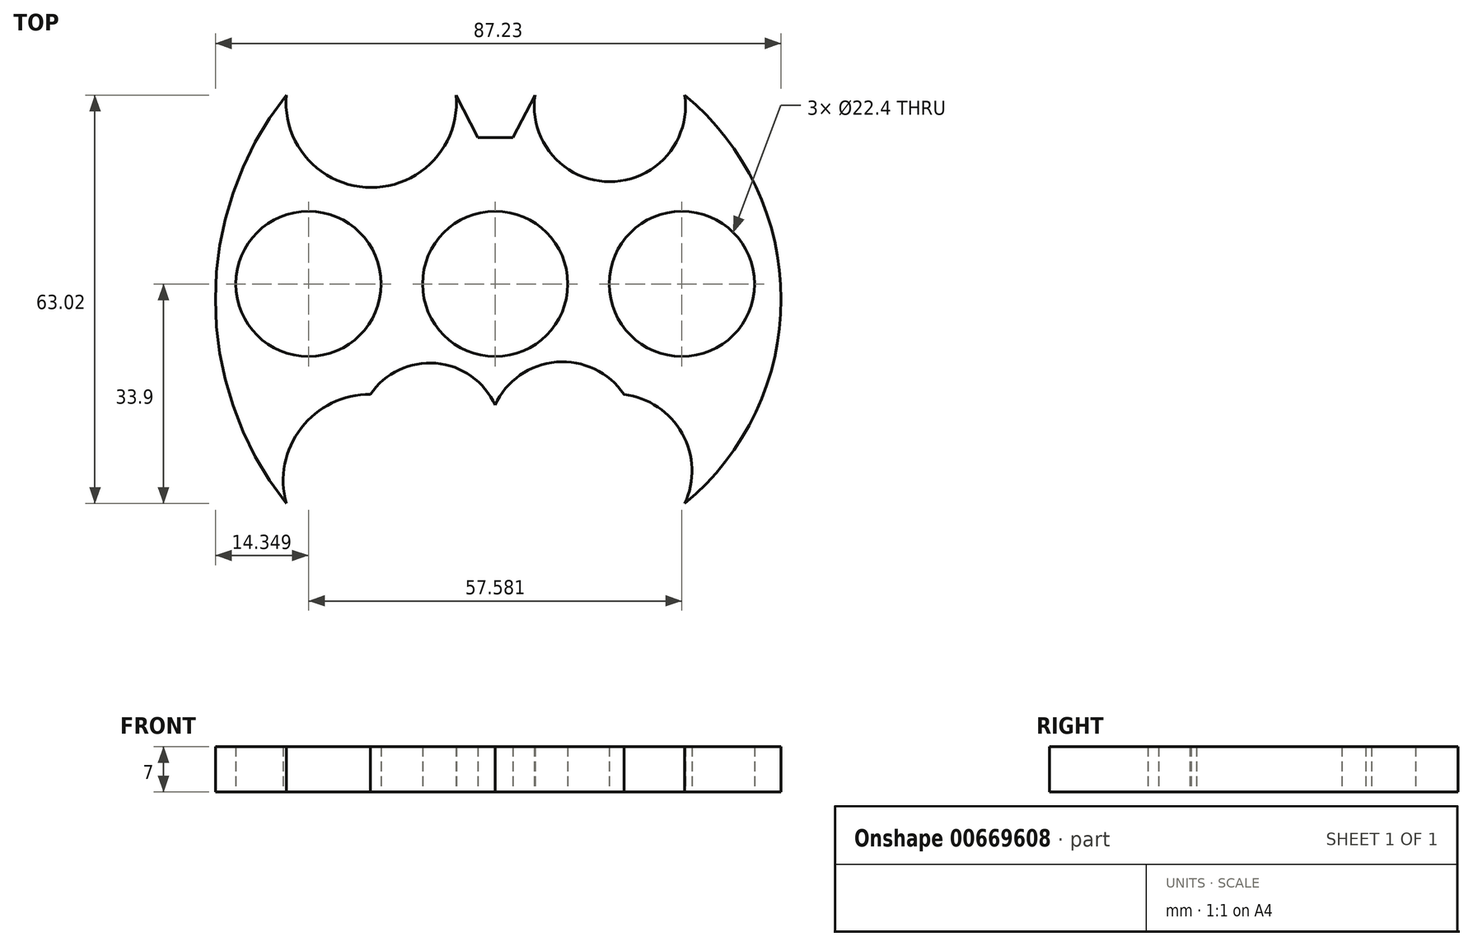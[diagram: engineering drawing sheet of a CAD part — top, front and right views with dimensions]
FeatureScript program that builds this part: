
annotation { "Feature Type Name" : "Feature", "Feature Type Description" : "" }
export const myFeature = defineFeature(function(context is Context, id is Id, definition is map)
    precondition{}
    {
        {
            var Q0;
            Q0=qCreatedBy(makeId("Top.planeOp"),FACE);
            var sketch = newSketch(context, id + "F0", { "sketchPlane" : qUnion([Q0])});
            skCircle(sketch, "E0", {"center": v(0, 0) * mm, "radius": 11.2 * mm});
            skArc(sketch, "E1", {"start": v(0, -18.71) * mm, "mid": v(-9.13, -12.24) * mm, "end": v(-19.24, -17.06) * mm});
            skArc(sketch, "E2", {"start": v(-19.24, -17.06) * mm, "mid": v(-29.92, -22.25) * mm, "end": v(-32.22, -33.9) * mm});
            skArc(sketch, "E3", {"start": v(-32.22, 29.12) * mm, "mid": v(-19.11, 14.87) * mm, "end": v(-6, 29.12) * mm});
            skArc(sketch, "E4", {"start": v(19.85, -17.06) * mm, "mid": v(9.44, -12.05) * mm, "end": v(0, -18.71) * mm});
            skArc(sketch, "E5", {"start": v(29.22, -33.9) * mm, "mid": v(28.84, -23.09) * mm, "end": v(19.85, -17.06) * mm});
            skArc(sketch, "E6", {"start": v(-32.22, 29.12) * mm, "mid": v(-43.14, -2.39) * mm, "end": v(-32.22, -33.9) * mm});
            skArc(sketch, "E7", {"start": v(6.13, 29.12) * mm, "mid": v(17.68, 15.78) * mm, "end": v(29.22, 29.12) * mm});
            skArc(sketch, "E8", {"start": v(29.22, -33.9) * mm, "mid": v(44.09, -2.39) * mm, "end": v(29.22, 29.12) * mm});
            skLineSegment(sketch, "E9", {"start": v(6.13, 29.12) * mm, "end": v(2.73, 22.56) * mm});
            skLineSegment(sketch, "E10", {"start": v(-2.65, 22.56) * mm, "end": v(-6, 29.12) * mm});
            skLineSegment(sketch, "E11", {"start": v(-2.65, 22.56) * mm, "end": v(2.73, 22.56) * mm});
            skCircle(sketch, "E12", {"center": v(-28.8, 0) * mm, "radius": 11.2 * mm});
            skCircle(sketch, "E13.2.0", {"center": v(28.8, 0) * mm, "radius": 11.2 * mm});
            skLineSegment(sketch, "E13.anchor1", {"start": v(0, 0) * mm, "end": v(-28.8, 0) * mm, "construction": true});
            skLineSegment(sketch, "E13.anchor2", {"start": v(0, 0) * mm, "end": v(28.8, 0) * mm, "construction": true});
            skPoint(sketch, "E14", {"position": v(-40, 0) * mm});
            skPoint(sketch, "E15", {"position": v(-17.6, 0) * mm});
            skSolve(sketch);
        }
        {
            var Q0;
            {var subQ0=sQuery(id+"F0.wireOp",EDGE,"E3");var subQ1=sQuery(id+"F0.wireOp",EDGE,"wIcN4tQ4-OL0U-KsKI-jLEZ-Zv3lfoWd9Mhj");var subQ2=makeQuery(id+"F0.imprint","INTERSECT",VERTEX,{"disambiguationData":[OD(0.0)],"derivedFrom":[subQ1,subQ0]});Q0=makeQuery(id+"F0.imprint","IMPRINT",FACE,{"disambiguationData":[TD([[makeQuery(id+"F0.imprint","IMPRINT",EDGE,{"disambiguationData":[TD([[subQ2,-1.0]])],"derivedFrom":subQ1}),1.0]])]});}
            var Q1;
            {var subQ0=sQuery(id+"F0.wireOp",EDGE,"E7");var subQ1=sQuery(id+"F0.wireOp",EDGE,"uIxHRKaC-fXGP-C11L-FGjw-L1SI6bDexqCe");var subQ2=makeQuery(id+"F0.imprint","INTERSECT",VERTEX,{"disambiguationData":[OD(0.0)],"derivedFrom":[subQ1,subQ0]});Q1=makeQuery(id+"F0.imprint","IMPRINT",FACE,{"disambiguationData":[TD([[makeQuery(id+"F0.imprint","IMPRINT",EDGE,{"disambiguationData":[TD([[subQ2,1.0]])],"derivedFrom":subQ1}),1.0]])]});}
            var Q2;
            Q2=makeQuery(id+"F0.imprint","IMPRINT",FACE,{"disambiguationData":[TD([[makeQuery(id+"F0.imprint","IMPRINT",EDGE,{"derivedFrom":sQuery(id+"F0.wireOp",EDGE,"E0")}),-1.0]])]});
            extrude(context, id + "F1", {"entities" : qUnion([Q0, Q1, Q2]), "depth" : 7 * mm, "offsetDistance" : 25 * mm});
        }
    });
